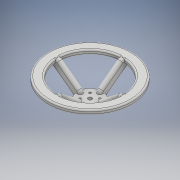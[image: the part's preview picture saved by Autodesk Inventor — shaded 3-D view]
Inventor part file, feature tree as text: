
AUTODESK INVENTOR PART (.ipt)
format: ipt  version: 2017 (Build 210142000, 142)  size: 381,952 bytes
history: native  units: mm
features: extrude x3, sketch x3, fillet x2, plane x1, pattern_circular x1
ambient origin geometry x8: Origin, YZ Plane, XZ Plane, XY Plane, X Axis, Y Axis, Z Axis, Center Point
bodies: Solid1 (feature_tree)
feature tree (10):
  extrude  "Extrusion1"  Depth=20.0mm
  plane  "Work Plane1"
  extrude  "Extrusion2"  Depth=50.0mm
  extrude  "Extrusion3"  Depth=10.0mm TaperAngle=0.0deg
  pattern_circular  "Circular Pattern1"  Count=3  [1 undecoded]
  fillet  "Fillet1"  Radius=170.0mm
  fillet  "Fillet2"  Radius=20.0mm
  sketch  "Sketch1"  dims[d0=8.0mm d1=20.0mm]
  sketch  "Sketch2"  dims[d2=20.0mm d3=50.0mm]
  sketch  "Sketch3"  dims[d4=4.5mm d5=10.0mm d6=0.0mm d7=30.0mm d8=170.0mm d9=20.0mm d10=10.0mm d11=0.0mm d12=10.0mm d13=0.0mm d14=40.0mm d15=360.0deg d17=5.0mm d18=3.0mm]
note: 1 required parameter value undecoded (feature->parameter linkage not recoverable at this tier; creation-order binding heuristic only, values carry confidence <= 0.55)
